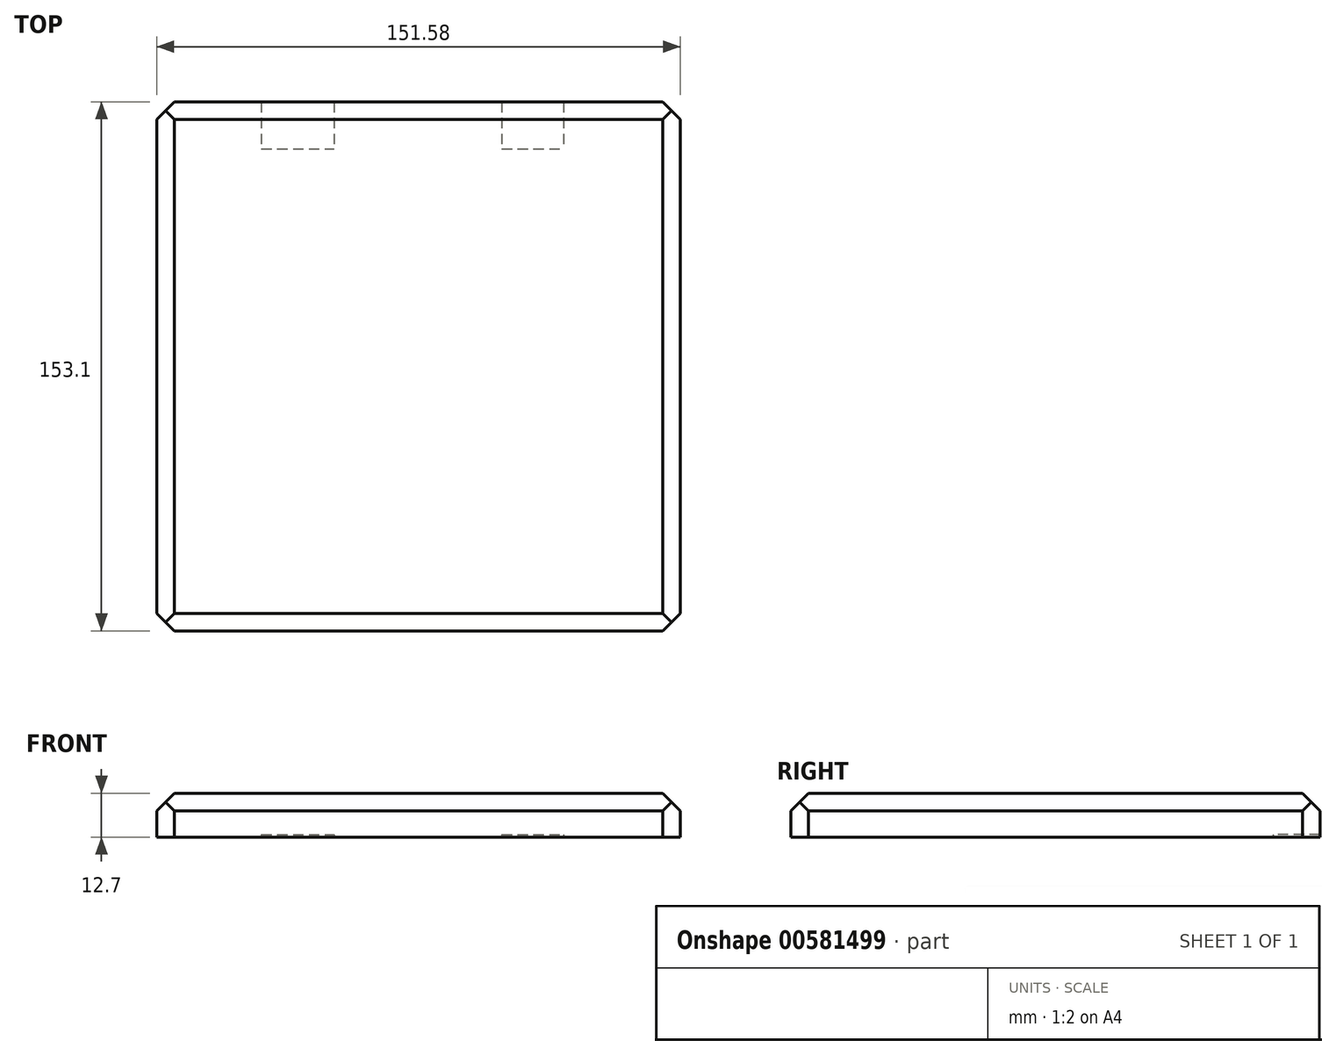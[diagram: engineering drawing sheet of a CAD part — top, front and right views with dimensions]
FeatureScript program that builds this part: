
annotation { "Feature Type Name" : "Feature", "Feature Type Description" : "" }
export const myFeature = defineFeature(function(context is Context, id is Id, definition is map)
    precondition{}
    {
        {
            var Q0;
            Q0=qCreatedBy(makeId("Top.planeOp"),FACE);
            var sketch = newSketch(context, id + "F0", { "sketchPlane" : qUnion([Q0])});
            skLineSegment(sketch, "E0.bottom", {"start": v(-75.89, 76.67) * mm, "end": v(75.69, 76.67) * mm});
            skLineSegment(sketch, "E0.top", {"start": v(-75.89, -76.43) * mm, "end": v(75.69, -76.43) * mm});
            skLineSegment(sketch, "E0.left", {"start": v(-75.89, 76.67) * mm, "end": v(-75.89, -76.43) * mm});
            skLineSegment(sketch, "E0.right", {"start": v(75.69, 76.67) * mm, "end": v(75.69, -76.43) * mm});
            skSolve(sketch);
        }
        {
            var Q0;
            Q0 = qSketchRegion(id + "F0", true);
            extrude(context, id + "F1", {"entities" : qUnion([Q0]), "endBound" : BoundingType.SYMMETRIC, "depth" : 12.7 * mm, "offsetDistance" : 25.4 * mm, "hasDraft" : true, "draftAngle" : 0 * degree});
        }
        {
            var Q0;
            Q0=makeQuery(id+"F1.opExtrude","CAP_EDGE",EDGE,{"disambiguationData":[OSD([sQuery(id+"F0.wireOp",EDGE,"E0.top")])],"isStart":false});
            chamfer(context, id + "F2", {"entities" : qUnion([Q0]), "width" : 5.08 * mm, "tangentPropagation" : true});
        }
        {
            var Q0;
            Q0=makeQuery(id+"F1.opExtrude","CAP_EDGE",EDGE,{"disambiguationData":[OSD([sQuery(id+"F0.wireOp",EDGE,"E0.bottom")])],"isStart":false});
            chamfer(context, id + "F3", {"entities" : qUnion([Q0]), "width" : 5.08 * mm, "tangentPropagation" : true});
        }
        {
            var Q0;
            Q0=makeQuery(id+"F1.opExtrude","CAP_EDGE",EDGE,{"disambiguationData":[OSD([sQuery(id+"F0.wireOp",EDGE,"E0.right")])],"isStart":false});
            chamfer(context, id + "F4", {"entities" : qUnion([Q0]), "width" : 5.08 * mm, "tangentPropagation" : true});
        }
        {
            var Q0;
            Q0=makeQuery(id+"F1.opExtrude","CAP_EDGE",EDGE,{"disambiguationData":[OSD([sQuery(id+"F0.wireOp",EDGE,"E0.left")])],"isStart":false});
            chamfer(context, id + "F5", {"entities" : qUnion([Q0]), "width" : 5.08 * mm, "tangentPropagation" : true});
        }
        {
            var Q0;
            Q0=makeQuery(id+"F1.opExtrude","CAP_FACE",FACE,{"disambiguationData":[OSD([sQuery(id+"F0.wireOp",EDGE,"E0.bottom"),sQuery(id+"F0.wireOp",EDGE,"E0.top"),sQuery(id+"F0.wireOp",EDGE,"E0.left"),sQuery(id+"F0.wireOp",EDGE,"E0.right")])],"isStart":true});
            var sketch = newSketch(context, id + "F6", { "sketchPlane" : qUnion([Q0])});
            skLineSegment(sketch, "E1.bottom", {"start": v(23.97, -76.67) * mm, "end": v(41.92, -76.67) * mm});
            skLineSegment(sketch, "E1.top", {"start": v(23.97, -63.13) * mm, "end": v(41.92, -63.13) * mm});
            skLineSegment(sketch, "E1.left", {"start": v(23.97, -76.67) * mm, "end": v(23.97, -63.13) * mm});
            skLineSegment(sketch, "E1.right", {"start": v(41.92, -76.67) * mm, "end": v(41.92, -63.13) * mm});
            skSolve(sketch);
        }
        {
            var Q0;
            Q0=makeQuery(id+"F6.imprint","IMPRINT",FACE,{"disambiguationData":[TD([[makeQuery(id+"F6.imprint","IMPRINT",EDGE,{"derivedFrom":sQuery(id+"F6.wireOp",EDGE,"E1.bottom")}),1.0]])]});
            extrude(context, id + "F7", {"entities" : qUnion([Q0]), "operationType" : NewBodyOperationType.REMOVE, "oppositeDirection" : true, "depth" : 0.76 * mm, "offsetDistance" : 25.4 * mm});
        }
        {
            var Q0;
            Q0=makeQuery(id+"F1.opExtrude","CAP_FACE",FACE,{"disambiguationData":[OSD([sQuery(id+"F0.wireOp",EDGE,"E0.bottom"),sQuery(id+"F0.wireOp",EDGE,"E0.top"),sQuery(id+"F0.wireOp",EDGE,"E0.left"),sQuery(id+"F0.wireOp",EDGE,"E0.right")])],"isStart":true});
            var sketch = newSketch(context, id + "F8", { "sketchPlane" : qUnion([Q0])});
            skLineSegment(sketch, "E2.bottom", {"start": v(-45.6, -76.67) * mm, "end": v(-24.57, -76.67) * mm});
            skLineSegment(sketch, "E2.top", {"start": v(-45.6, -63.13) * mm, "end": v(-24.57, -63.13) * mm});
            skLineSegment(sketch, "E2.left", {"start": v(-45.6, -76.67) * mm, "end": v(-45.6, -63.13) * mm});
            skLineSegment(sketch, "E2.right", {"start": v(-24.57, -76.67) * mm, "end": v(-24.57, -63.13) * mm});
            skSolve(sketch);
        }
        {
            var Q0;
            Q0=makeQuery(id+"F8.imprint","IMPRINT",FACE,{"disambiguationData":[TD([[makeQuery(id+"F8.imprint","IMPRINT",EDGE,{"derivedFrom":sQuery(id+"F8.wireOp",EDGE,"E2.bottom")}),1.0]])]});
            extrude(context, id + "F9", {"entities" : qUnion([Q0]), "operationType" : NewBodyOperationType.REMOVE, "oppositeDirection" : true, "depth" : 0.76 * mm, "offsetDistance" : 25.4 * mm});
        }
        {
            var Q0;
            {var subQ0=makeQuery(id+"F1.opExtrude","SWEPT_EDGE",EDGE,{"disambiguationData":[OSD([sQuery(id+"F0.wireOp",EDGE,"E0.top"),sQuery(id+"F0.wireOp",EDGE,"E0.right")])]});Q0=makeQuery(id+"F1.*.booleanUnion.opBoolean","MERGE",EDGE,{"derivedFrom":[makeQuery(id+"F1.*.split.splitOp","SPLIT",EDGE,{"derivedFrom":subQ0,"isFromBackBody":true}),makeQuery(id+"F1.*.split.splitOp","SPLIT",EDGE,{"derivedFrom":subQ0})]});}
            chamfer(context, id + "F10", {"entities" : qUnion([Q0]), "width" : 5.08 * mm, "tangentPropagation" : true});
        }
        {
            var Q0;
            {var subQ0=makeQuery(id+"F1.opExtrude","SWEPT_EDGE",EDGE,{"disambiguationData":[OSD([sQuery(id+"F0.wireOp",EDGE,"E0.bottom"),sQuery(id+"F0.wireOp",EDGE,"E0.right")])]});Q0=makeQuery(id+"F1.*.booleanUnion.opBoolean","MERGE",EDGE,{"derivedFrom":[makeQuery(id+"F1.*.split.splitOp","SPLIT",EDGE,{"derivedFrom":subQ0,"isFromBackBody":true}),makeQuery(id+"F1.*.split.splitOp","SPLIT",EDGE,{"derivedFrom":subQ0})]});}
            chamfer(context, id + "F11", {"entities" : qUnion([Q0]), "width" : 5.08 * mm, "tangentPropagation" : true});
        }
        {
            var Q0;
            {var subQ0=makeQuery(id+"F1.opExtrude","SWEPT_EDGE",EDGE,{"disambiguationData":[OSD([sQuery(id+"F0.wireOp",EDGE,"E0.bottom"),sQuery(id+"F0.wireOp",EDGE,"E0.left")])]});Q0=makeQuery(id+"F1.*.booleanUnion.opBoolean","MERGE",EDGE,{"derivedFrom":[makeQuery(id+"F1.*.split.splitOp","SPLIT",EDGE,{"derivedFrom":subQ0,"isFromBackBody":true}),makeQuery(id+"F1.*.split.splitOp","SPLIT",EDGE,{"derivedFrom":subQ0})]});}
            chamfer(context, id + "F12", {"entities" : qUnion([Q0]), "width" : 5.08 * mm, "tangentPropagation" : true});
        }
        {
            var Q0;
            {var subQ0=makeQuery(id+"F1.opExtrude","SWEPT_EDGE",EDGE,{"disambiguationData":[OSD([sQuery(id+"F0.wireOp",EDGE,"E0.top"),sQuery(id+"F0.wireOp",EDGE,"E0.left")])]});Q0=makeQuery(id+"F1.*.booleanUnion.opBoolean","MERGE",EDGE,{"derivedFrom":[makeQuery(id+"F1.*.split.splitOp","SPLIT",EDGE,{"derivedFrom":subQ0,"isFromBackBody":true}),makeQuery(id+"F1.*.split.splitOp","SPLIT",EDGE,{"derivedFrom":subQ0})]});}
            chamfer(context, id + "F13", {"entities" : qUnion([Q0]), "width" : 5.08 * mm, "tangentPropagation" : true});
        }
    });
